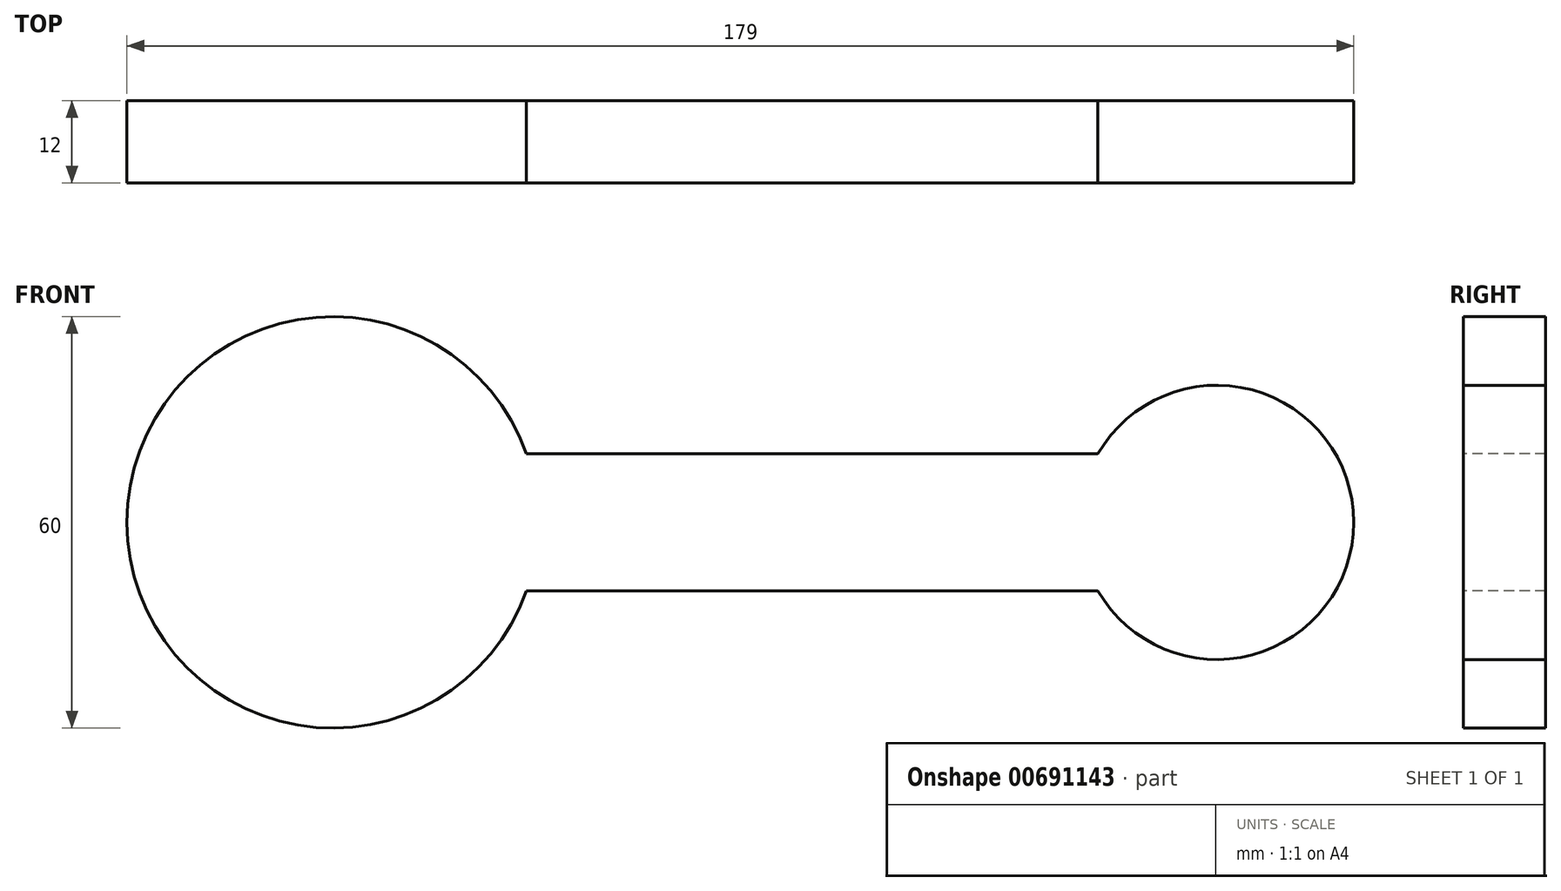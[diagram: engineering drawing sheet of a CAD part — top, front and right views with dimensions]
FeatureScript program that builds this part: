
annotation { "Feature Type Name" : "Feature", "Feature Type Description" : "" }
export const myFeature = defineFeature(function(context is Context, id is Id, definition is map)
    precondition{}
    {
        {
            var Q0;
            Q0=qCreatedBy(makeId("Front.planeOp"),FACE);
            var sketch = newSketch(context, id + "F0", { "sketchPlane" : qUnion([Q0])});
            skLineSegment(sketch, "E0.bottom", {"start": v(-64.5, 10) * mm, "end": v(64.5, 10) * mm});
            skLineSegment(sketch, "E0.top", {"start": v(-64.5, -10) * mm, "end": v(64.5, -10) * mm});
            skLineSegment(sketch, "E0.left", {"start": v(-64.5, 10) * mm, "end": v(-64.5, -10) * mm});
            skLineSegment(sketch, "E0.right", {"start": v(64.5, 10) * mm, "end": v(64.5, -10) * mm});
            skPoint(sketch, "E0.middle", {"position": v(0, 0) * mm});
            skCircle(sketch, "E1", {"center": v(-64.5, 0) * mm, "radius": 30 * mm});
            skCircle(sketch, "E2.MirrorC", {"center": v(64.5, 0) * mm, "radius": 20 * mm});
            skSolve(sketch);
        }
        {
            var Q0;
            Q0 = qSketchRegion(id + "F0", true);
            extrude(context, id + "F1", {"entities" : qUnion([Q0]), "oppositeDirection" : true, "depth" : 12 * mm, "offsetDistance" : 25 * mm});
        }
    });
